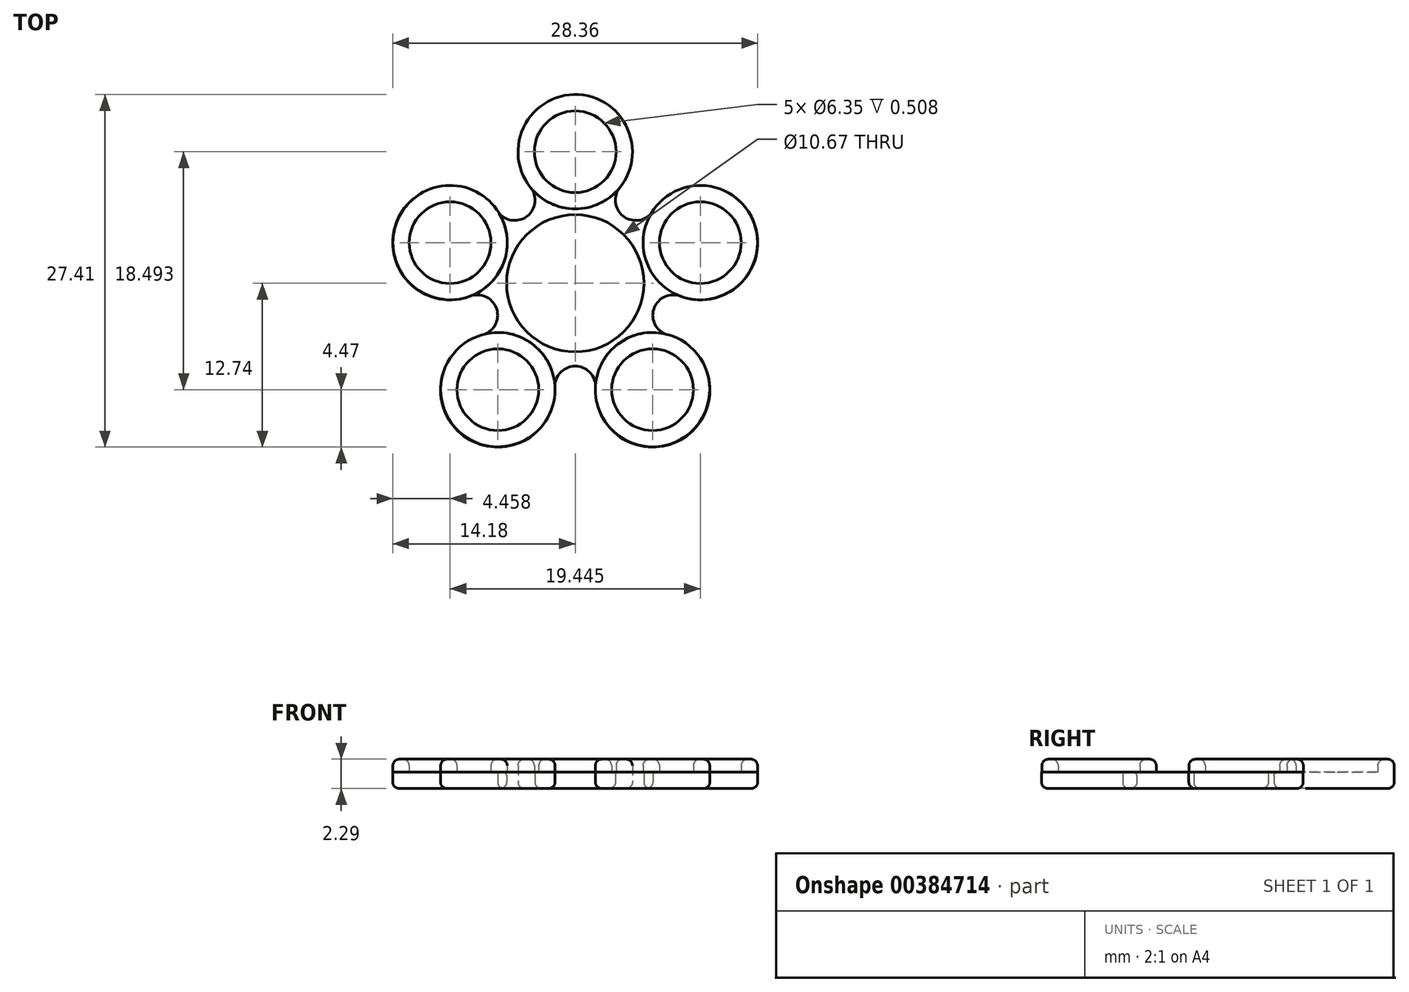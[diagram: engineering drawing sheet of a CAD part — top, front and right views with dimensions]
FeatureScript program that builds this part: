
annotation { "Feature Type Name" : "Feature", "Feature Type Description" : "" }
export const myFeature = defineFeature(function(context is Context, id is Id, definition is map)
    precondition{}
    {
        {
            var Q0;
            Q0=qCreatedBy(makeId("Top.planeOp"),FACE);
            var sketch = newSketch(context, id + "F0", { "sketchPlane" : qUnion([Q0])});
            skArc(sketch, "E0", {"start": v(3.47, 7.45) * mm, "mid": v(0, 14.67) * mm, "end": v(-3.47, 7.45) * mm});
            skArc(sketch, "E1.1.0", {"start": v(-6.02, 5.6) * mm, "mid": v(-13.96, 4.52) * mm, "end": v(-8.17, -1) * mm});
            skArc(sketch, "E1.2.0", {"start": v(-7.2, -4) * mm, "mid": v(-8.63, -11.9) * mm, "end": v(-1.58, -8.09) * mm});
            skArc(sketch, "E1.3.0", {"start": v(1.58, -8.09) * mm, "mid": v(8.63, -11.9) * mm, "end": v(7.2, -4) * mm});
            skArc(sketch, "E1.4.0", {"start": v(8.17, -1) * mm, "mid": v(13.96, 4.52) * mm, "end": v(6.02, 5.6) * mm});
            skPoint(sketch, "E1.center", {"position": v(0, -0.01) * mm});
            skArc(sketch, "E2", {"start": v(-6.02, 5.6) * mm, "mid": v(-3.78, 5.18) * mm, "end": v(-3.47, 7.45) * mm});
            skCircle(sketch, "E3", {"center": v(0, 0) * mm, "radius": 5.33 * mm});
            skArc(sketch, "E4.1.0", {"start": v(-7.2, -4) * mm, "mid": v(-6.1, -2) * mm, "end": v(-8.17, -1) * mm});
            skArc(sketch, "E4.2.0", {"start": v(1.58, -8.09) * mm, "mid": v(0, -6.44) * mm, "end": v(-1.58, -8.09) * mm});
            skArc(sketch, "E4.3.0", {"start": v(8.17, -1) * mm, "mid": v(6.1, -2) * mm, "end": v(7.2, -4) * mm});
            skArc(sketch, "E4.4.0", {"start": v(3.47, 7.45) * mm, "mid": v(3.78, 5.18) * mm, "end": v(6.02, 5.6) * mm});
            skSolve(sketch);
        }
        {
            var Q0;
            Q0=qSketchRegion(id+"F0",true);
            extrude(context, id + "F1", {"entities" : qUnion([Q0]), "depth" : 1.27 * mm, "offsetDistance" : 25.4 * mm});
        }
        {
            var Q0;
            Q0=makeQuery(id+"F1.opExtrude","CAP_FACE",FACE,{"disambiguationData":[OSD([sQuery(id+"F0.wireOp",EDGE,"E0"),sQuery(id+"F0.wireOp",EDGE,"E1.1.0"),sQuery(id+"F0.wireOp",EDGE,"E1.2.0"),sQuery(id+"F0.wireOp",EDGE,"E1.3.0"),sQuery(id+"F0.wireOp",EDGE,"E1.4.0"),sQuery(id+"F0.wireOp",EDGE,"E2"),sQuery(id+"F0.wireOp",EDGE,"E3"),sQuery(id+"F0.wireOp",EDGE,"E4.1.0"),sQuery(id+"F0.wireOp",EDGE,"E4.2.0"),sQuery(id+"F0.wireOp",EDGE,"E4.3.0"),sQuery(id+"F0.wireOp",EDGE,"E4.4.0")])],"isStart":false});
            var sketch = newSketch(context, id + "F2", { "sketchPlane" : qUnion([Q0])});
            skCircle(sketch, "E5", {"center": v(0, 10.22) * mm, "radius": 4.45 * mm});
            skCircle(sketch, "E6", {"center": v(0, 10.22) * mm, "radius": 3.17 * mm});
            skCircle(sketch, "E7.1.0", {"center": v(-9.72, 3.16) * mm, "radius": 4.45 * mm});
            skCircle(sketch, "E7.1.1", {"center": v(-9.72, 3.16) * mm, "radius": 3.17 * mm});
            skCircle(sketch, "E7.2.0", {"center": v(-6, -8.27) * mm, "radius": 4.45 * mm});
            skCircle(sketch, "E7.2.1", {"center": v(-6, -8.27) * mm, "radius": 3.17 * mm});
            skCircle(sketch, "E7.3.0", {"center": v(6, -8.27) * mm, "radius": 4.45 * mm});
            skCircle(sketch, "E7.3.1", {"center": v(6, -8.27) * mm, "radius": 3.17 * mm});
            skCircle(sketch, "E7.4.0", {"center": v(9.72, 3.16) * mm, "radius": 4.45 * mm});
            skCircle(sketch, "E7.4.1", {"center": v(9.72, 3.16) * mm, "radius": 3.17 * mm});
            skPoint(sketch, "E7.center", {"position": v(0, 0) * mm});
            skSolve(sketch);
        }
        {
            var Q0;
            Q0 = qSketchRegion(id + "F2", true);
            extrude(context, id + "F3", {"entities" : qUnion([Q0]), "operationType" : NewBodyOperationType.ADD, "depth" : 1.02 * mm, "offsetDistance" : 25.4 * mm});
        }
        {
            var Q0;
            Q0=makeQuery(id+"F3.opExtrude","CAP_FACE",FACE,{"disambiguationData":[OSD([sQuery(id+"F2.wireOp",EDGE,"E5"),sQuery(id+"F2.wireOp",EDGE,"E6")])],"isStart":false});
            var Q1;
            Q1=makeQuery(id+"F3.opExtrude","CAP_FACE",FACE,{"disambiguationData":[OSD([sQuery(id+"F2.wireOp",EDGE,"E7.1.0"),sQuery(id+"F2.wireOp",EDGE,"E7.1.1")])],"isStart":false});
            var Q2;
            Q2=makeQuery(id+"F3.opExtrude","CAP_FACE",FACE,{"disambiguationData":[OSD([sQuery(id+"F2.wireOp",EDGE,"E7.4.0"),sQuery(id+"F2.wireOp",EDGE,"E7.4.1")])],"isStart":false});
            var Q3;
            Q3=makeQuery(id+"F3.opExtrude","CAP_FACE",FACE,{"disambiguationData":[OSD([sQuery(id+"F2.wireOp",EDGE,"E7.2.0"),sQuery(id+"F2.wireOp",EDGE,"E7.2.1")])],"isStart":false});
            var Q4;
            Q4=makeQuery(id+"F3.opExtrude","CAP_FACE",FACE,{"disambiguationData":[OSD([sQuery(id+"F2.wireOp",EDGE,"E7.3.0"),sQuery(id+"F2.wireOp",EDGE,"E7.3.1")])],"isStart":false});
            fillet(context, id + "F4", {"entities" : qUnion([Q0, Q1, Q2, Q3, Q4]), "radius" : 0.5 * mm, "tangentPropagation" : true, "allowEdgeOverflow" : false});
        }
        {
            var Q0;
            Q0=makeQuery(id+"F1.opExtrude","CAP_FACE",FACE,{"disambiguationData":[OSD([sQuery(id+"F0.wireOp",EDGE,"E0"),sQuery(id+"F0.wireOp",EDGE,"E1.1.0"),sQuery(id+"F0.wireOp",EDGE,"E1.2.0"),sQuery(id+"F0.wireOp",EDGE,"E1.3.0"),sQuery(id+"F0.wireOp",EDGE,"E1.4.0"),sQuery(id+"F0.wireOp",EDGE,"E2"),sQuery(id+"F0.wireOp",EDGE,"E3"),sQuery(id+"F0.wireOp",EDGE,"E4.1.0"),sQuery(id+"F0.wireOp",EDGE,"E4.2.0"),sQuery(id+"F0.wireOp",EDGE,"E4.3.0"),sQuery(id+"F0.wireOp",EDGE,"E4.4.0")])],"isStart":true});
            fillet(context, id + "F5", {"entities" : qUnion([Q0]), "radius" : 0.5 * mm, "tangentPropagation" : true, "allowEdgeOverflow" : false});
        }
        {
            var Q0;
            Q0=makeQuery(id+"F1.opExtrude","CAP_EDGE",EDGE,{"disambiguationData":[OSD([sQuery(id+"F0.wireOp",EDGE,"E3")])],"isStart":false});
            fillet(context, id + "F6", {"entities" : qUnion([Q0]), "radius" : 0.25 * mm, "tangentPropagation" : true, "allowEdgeOverflow" : false});
        }
    });
